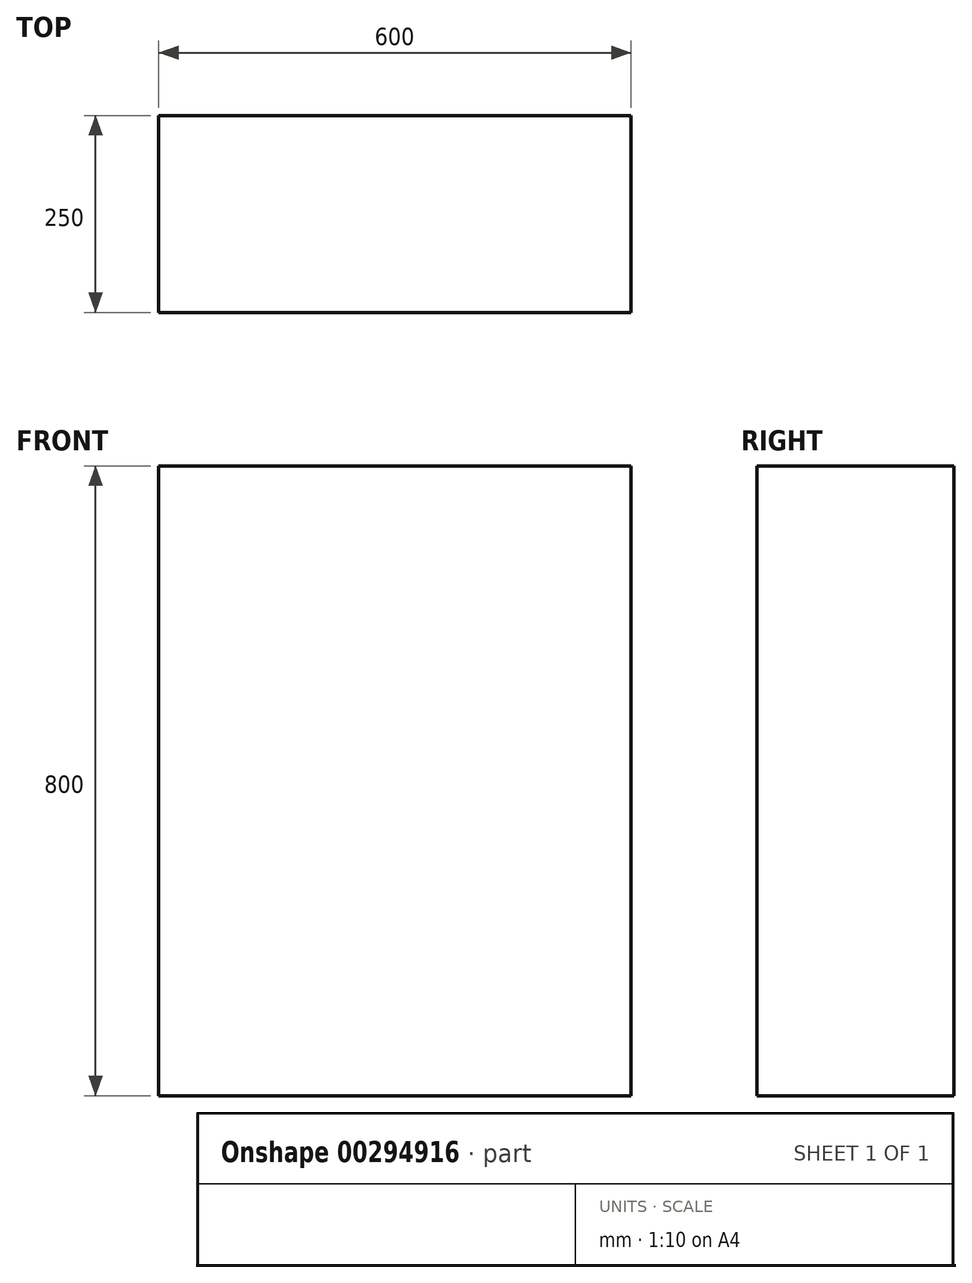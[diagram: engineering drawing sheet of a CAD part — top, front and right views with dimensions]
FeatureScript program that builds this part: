
annotation { "Feature Type Name" : "Feature", "Feature Type Description" : "" }
export const myFeature = defineFeature(function(context is Context, id is Id, definition is map)
    precondition{}
    {
        {
            var Q0;
            Q0=qCreatedBy(makeId("Front.planeOp"),FACE);
            var sketch = newSketch(context, id + "F0", { "sketchPlane" : qUnion([Q0])});
            skLineSegment(sketch, "E0.bottom", {"start": v(300, 400) * mm, "end": v(-300, 400) * mm});
            skLineSegment(sketch, "E0.top", {"start": v(300, -400) * mm, "end": v(-300, -400) * mm});
            skLineSegment(sketch, "E0.left", {"start": v(300, 400) * mm, "end": v(300, -400) * mm});
            skLineSegment(sketch, "E0.right", {"start": v(-300, 400) * mm, "end": v(-300, -400) * mm});
            skPoint(sketch, "E0.middle", {"position": v(0, 0) * mm});
            skSolve(sketch);
        }
        {
            var Q0;
            Q0=makeQuery(id+"F0.imprint","IMPRINT",FACE,{"disambiguationData":[TD([[makeQuery(id+"F0.imprint","IMPRINT",EDGE,{"derivedFrom":sQuery(id+"F0.wireOp",EDGE,"E0.bottom")}),1.0]])]});
            extrude(context, id + "F1", {"entities" : qUnion([Q0]), "depth" : 250 * mm, "offsetDistance" : 25 * mm});
        }
    });
